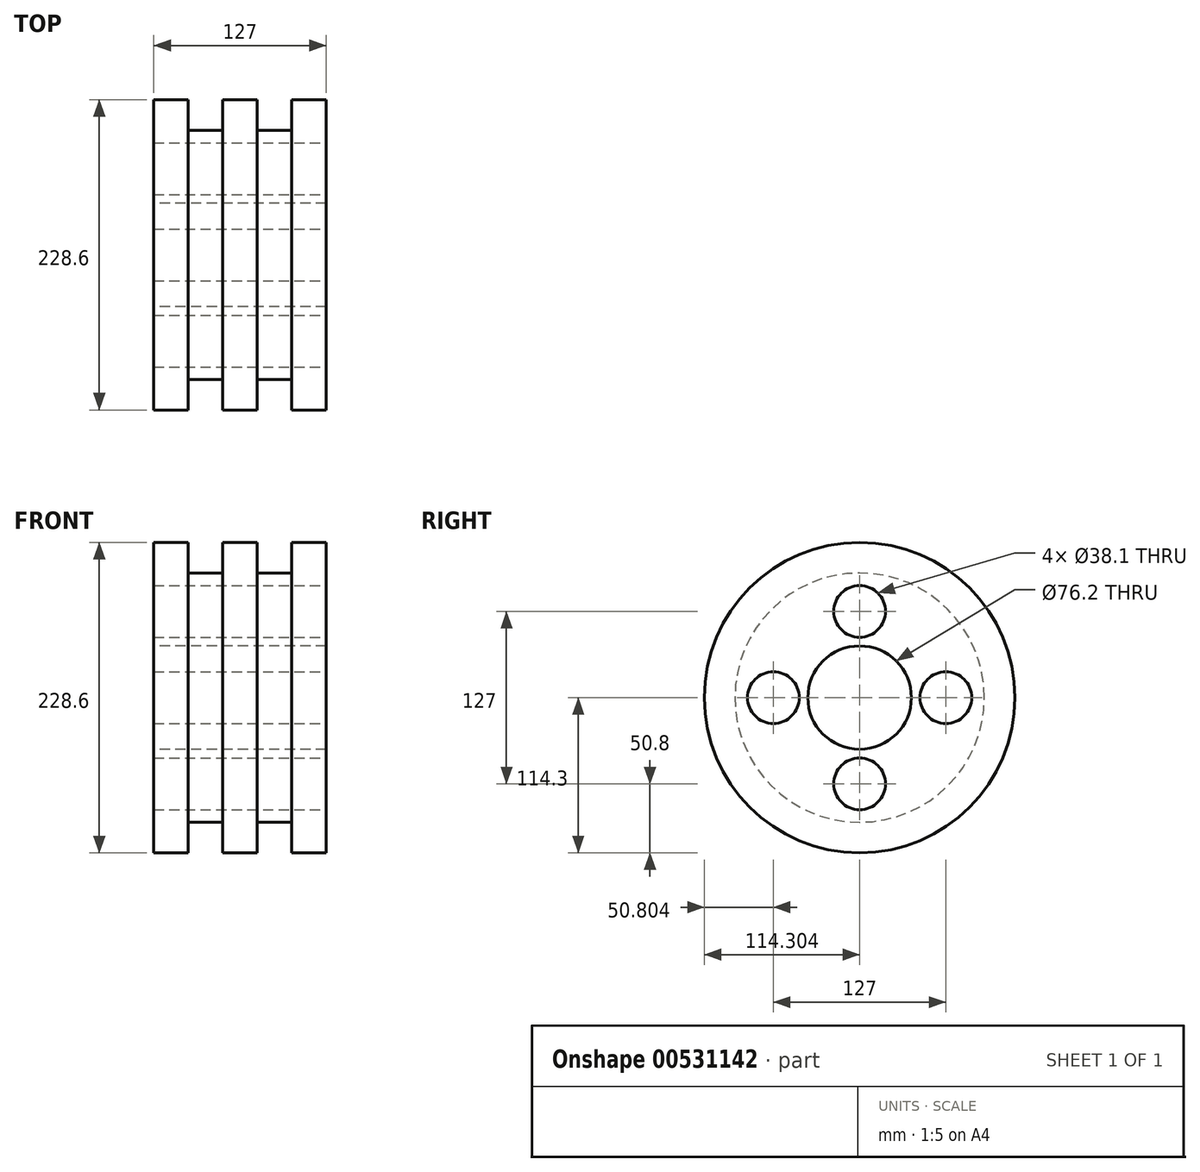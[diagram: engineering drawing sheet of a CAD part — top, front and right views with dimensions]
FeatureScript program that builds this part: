
annotation { "Feature Type Name" : "Feature", "Feature Type Description" : "" }
export const myFeature = defineFeature(function(context is Context, id is Id, definition is map)
    precondition{}
    {
        {
            var Q0;
            Q0=qCreatedBy(makeId("Top.planeOp"),FACE);
            var sketch = newSketch(context, id + "F0", { "sketchPlane" : qUnion([Q0])});
            skLineSegment(sketch, "E0", {"start": v(-62.74, 46.43) * mm, "end": v(-37.34, 46.43) * mm});
            skLineSegment(sketch, "E1", {"start": v(-37.34, 46.43) * mm, "end": v(-37.34, 23.95) * mm});
            skLineSegment(sketch, "E2", {"start": v(-37.34, 23.95) * mm, "end": v(-11.94, 23.95) * mm});
            skLineSegment(sketch, "E3", {"start": v(-11.94, 23.95) * mm, "end": v(-11.94, 46.43) * mm});
            skLineSegment(sketch, "E4", {"start": v(-11.94, 46.43) * mm, "end": v(13.46, 46.43) * mm});
            skLineSegment(sketch, "E5", {"start": v(13.46, 46.43) * mm, "end": v(13.46, 23.95) * mm});
            skLineSegment(sketch, "E6", {"start": v(13.46, 23.95) * mm, "end": v(38.86, 23.95) * mm});
            skLineSegment(sketch, "E7", {"start": v(38.86, 23.95) * mm, "end": v(38.86, 46.43) * mm});
            skLineSegment(sketch, "E8", {"start": v(38.86, 46.43) * mm, "end": v(64.26, 46.43) * mm});
            skLineSegment(sketch, "E9", {"start": v(64.26, 46.43) * mm, "end": v(64.26, -29.77) * mm});
            skLineSegment(sketch, "E10", {"start": v(64.26, -29.77) * mm, "end": v(-62.74, -29.77) * mm});
            skLineSegment(sketch, "E11", {"start": v(-62.74, -29.77) * mm, "end": v(-62.74, 46.43) * mm});
            skLineSegment(sketch, "E12", {"start": v(-62.74, -29.77) * mm, "end": v(-62.74, -67.87) * mm});
            skLineSegment(sketch, "E13", {"start": v(-62.74, -67.87) * mm, "end": v(64.26, -67.87) * mm, "construction": true});
            skSolve(sketch);
        }
        {
            var Q0;
            Q0 = qSketchRegion(id + "F0", true);
            var Q1;
            Q1=sQuery(id+"F0.wireOp",EDGE,"E13");
            revolve(context, id + "F1", {"entities" : qUnion([Q0]), "axis" : qUnion([Q1]), "revolveType" : RevolveType.FULL});
        }
        {
            var Q0;
            Q0=makeQuery(id+"F1.opRevolve","SWEPT_FACE",FACE,{"disambiguationData":[OSD([sQuery(id+"F0.wireOp",EDGE,"E9")])]});
            var sketch = newSketch(context, id + "F2", { "sketchPlane" : qUnion([Q0])});
            skLineSegment(sketch, "E14", {"start": v(-105.97, 0) * mm, "end": v(-131.37, 0) * mm});
            skLineSegment(sketch, "E15", {"start": v(-67.87, -38.1) * mm, "end": v(-67.87, -63.5) * mm});
            skPoint(sketch, "E15.startSnap0", {"position": v(-67.87, 0) * mm});
            skLineSegment(sketch, "E16", {"start": v(-67.87, 38.1) * mm, "end": v(-67.87, 63.5) * mm});
            skLineSegment(sketch, "E17", {"start": v(-29.77, 0) * mm, "end": v(-4.37, 0) * mm});
            skCircle(sketch, "E18", {"center": v(-67.87, 63.5) * mm, "radius": 19.05 * mm});
            skCircle(sketch, "E19", {"center": v(-131.37, 0) * mm, "radius": 19.05 * mm});
            skCircle(sketch, "E20", {"center": v(-67.87, -63.5) * mm, "radius": 19.05 * mm});
            skCircle(sketch, "E21", {"center": v(-4.37, 0) * mm, "radius": 19.05 * mm});
            skSolve(sketch);
        }
        {
            var Q0;
            Q0 = qSketchRegion(id + "F2", true);
            extrude(context, id + "F3", {"entities" : qUnion([Q0]), "operationType" : NewBodyOperationType.REMOVE, "endBound" : BoundingType.UP_TO_NEXT, "oppositeDirection" : true, "depth" : 127 * mm, "offsetDistance" : 25.4 * mm});
        }
    });
